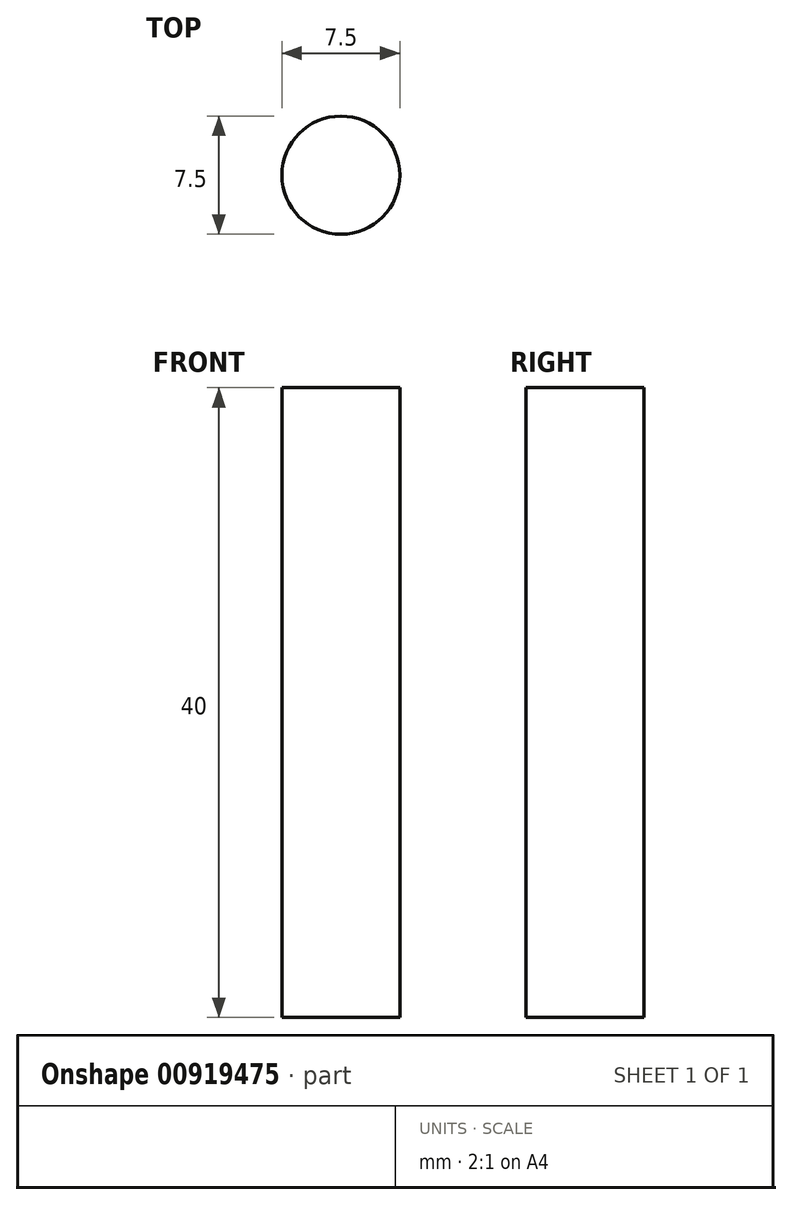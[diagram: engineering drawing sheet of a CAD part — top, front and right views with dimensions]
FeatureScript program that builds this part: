
annotation { "Feature Type Name" : "Feature", "Feature Type Description" : "" }
export const myFeature = defineFeature(function(context is Context, id is Id, definition is map)
    precondition{}
    {
        {
            var Q0;
            Q0=qCreatedBy(makeId("Top.planeOp"),FACE);
            var sketch = newSketch(context, id + "F0", { "sketchPlane" : qUnion([Q0])});
            skCircle(sketch, "E0", {"center": v(0, 0) * mm, "radius": 3.75 * mm});
            skSolve(sketch);
        }
        {
            var Q0;
            Q0 = qSketchRegion(id + "F0", true);
            extrude(context, id + "F1", {"entities" : qUnion([Q0]), "depth" : 40 * mm, "offsetDistance" : 25 * mm});
        }
    });
